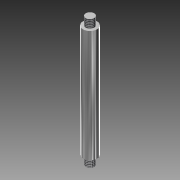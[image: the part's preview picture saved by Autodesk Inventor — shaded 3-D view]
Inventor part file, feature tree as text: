
AUTODESK INVENTOR PART (.ipt)
format: ipt  version: 2012 (Build 160160000, 160)  size: 80,896 bytes
history: native  units: mm
features: extrude x3, sketch x3, thread x2
ambient origin geometry x8: Origin, YZ Plane, XZ Plane, XY Plane, X Axis, Y Axis, Z Axis, Center Point
bodies: Solid1 (feature_tree)
feature tree (8):
  extrude  "Extrusion1"  Depth=40.0mm TaperAngle=0.0deg
  extrude  "Extrusion2"  Depth=3.0mm TaperAngle=0.0deg
  thread  "Thread1"  [1 undecoded]
  extrude  "Extrusion3"  Depth=3.0mm TaperAngle=0.0deg
  thread  "Thread2"  [1 undecoded]
  sketch  "Sketch1"  dims[d0=5.0mm d1=40.0mm d2=0.0mm]
  sketch  "Sketch2"  dims[d3=3.0mm d4=3.0mm d5=0.0mm d6=10.0mm d7=0.0mm]
  sketch  "Sketch3"  dims[d8=3.0mm d9=3.0mm d10=0.0mm d11=10.0mm d12=0.0mm]
note: 2 required parameter values undecoded (feature->parameter linkage not recoverable at this tier; creation-order binding heuristic only, values carry confidence <= 0.55)
